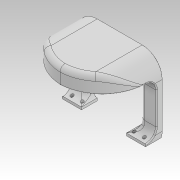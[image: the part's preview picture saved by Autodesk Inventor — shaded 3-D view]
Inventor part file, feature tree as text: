
AUTODESK INVENTOR PART (.ipt)
format: ipt  version: 2020 (Build 240168000, 168)  size: 1,175,552 bytes
history: native  units: mm
features: sketch x16, extrude x14, projected_geometry x6, fillet x4, plane x4, mirror x2, other x2, chamfer x2, revolve x1
ambient origin geometry x8: Origin, YZ Plane, XZ Plane, XY Plane, X Axis, Y Axis, Z Axis, Center Point
bodies: Solid1 (feature_tree)
feature tree (51):
  extrude  "Extrusion1"  Depth=170.0mm
  extrude  "Extrusion2"  Depth=33.0mm
  extrude  "Extrusion3"  Depth=12.0mm
  sketch  "Sketch4"  dims[d8=20.0mm d9=0.0mm d10=0.0mm]
  revolve  "Revolution1"  [1 undecoded]
  extrude  "Extrusion4"  Depth=47.55mm
  extrude  "Extrusion5"  Depth=3.0mm
  fillet  "Fillet1"  Radius=1.0mm
  extrude  "Extrusion8"  Depth=17.5mm
  mirror  "Mirror1"
  extrude  "Extrusion6"  TaperAngle=90.0deg  [1 undecoded]
  extrude  "Extrusion7"  Depth=0.6mm
  extrude  "Extrusion9"  Depth=5.2mm
  other  "Spur Gear Teeth1"
  extrude  "Extrusion10"  Depth=1.0mm
  extrude  "Extrusion11"  Depth=25.0mm
  mirror  "Mirror2"
  fillet  "Fillet3"  Radius=19.0mm
  plane  "Work Plane2"
  extrude  "Extrusion12"  Depth=15.0mm
  extrude  "Extrusion13"  Depth=104.0mm
  plane  "Work Plane3"
  sketch  "Sketch15"  dims[d37=8.0mm d38=45.0deg d39=6.4mm d40=40.0mm d42=360.0deg d44=12.5mm d45=0.0mm]
  plane  "Work Plane4"
  extrude  "Extrusion14"  TaperAngle=45.0deg  [1 undecoded]
  fillet  "Fillet4"  Radius=6.4mm
  fillet  "Fillet5"  Radius=40.0mm
  chamfer  "Chamfer1"  Distance=12.5mm
  chamfer  "Chamfer2"  Distance=5.0mm
  sketch  "Sketch1"  dims[d0=170.0mm d1=170.0mm]
  sketch  "Sketch2"  dims[d2=40.0mm d3=33.0mm]
  projected_geometry  "Projected Loop1"
  projected_geometry  "Projected Loop2"
  sketch  "Sketch3"  dims[d4=120.0mm d5=0.0mm d7=12.0mm]
  projected_geometry  "Projected Loop3"
  sketch  "Sketch5"  dims[d11=0.0mm d12=0.0mm d13=47.55mm]
  sketch  "Sketch6"  dims[d14=10.1mm d15=3.0mm d16=1.0mm]
  projected_geometry  "Projected Loop4"
  sketch  "Sketch7"  dims[d17=40.075mm d18=17.5mm]
  sketch  "Sketch8"  dims[d19=65.0mm d20=90.0deg]
  sketch  "Sketch9"  dims[d21=8.05mm d22=0.6mm]
  sketch  "Sketch10"  dims[d23=1.5mm d25=5.2mm]
  other  "Spur Gear2"
  sketch  "Sketch11"  dims[d26=1.0mm d27=1.0mm]
  projected_geometry  "Projected Loop5"
  sketch  "Sketch12"  dims[d29=25.0mm d30=2.0mm d31=19.0mm]
  plane  "Work Plane1"
  sketch  "Sketch13"  dims[d32=38.0mm d33=15.0mm]
  sketch  "Sketch14"  dims[d34=5.0mm d35=0.0mm d36=104.0mm]
  projected_geometry  "Projected Loop6"
  sketch  "Sketch16"  dims[d46=10.0mm d47=5.0mm d48=0.0mm d49=137.0mm d50=0.0mm d51=4.2mm d52=12.0mm d53=7.0mm d54=5.0mm d55=17.0mm d56=0.0mm d57=0.0mm d58=35.0mm d59=72.5mm d60=5.0mm d61=0.0mm d62=75.0mm d63=5.0mm d64=0.0mm d65=5.0mm d66=0.0mm d67=16.0mm d69=10.0mm d70=-2.5mm d71=6.0mm d72=42.0mm d73=0.0mm d74=75.0mm d75=5.0mm d76=92.0mm d77=8.0mm d78=0.0mm d79=12.0mm d80=4.363323mm d81=15.0mm d82=6.4mm d83=51.5mm d84=0.0mm d85=0.5mm d86=2.0mm d87=0.5mm d88=2.0mm d89=45.0deg d90=60.0deg d91=9.599311mm d92=9.599311mm d93=0.5mm d94=2.0mm d95=45.0deg]
note: 3 required parameter values undecoded (feature->parameter linkage not recoverable at this tier; creation-order binding heuristic only, values carry confidence <= 0.55)